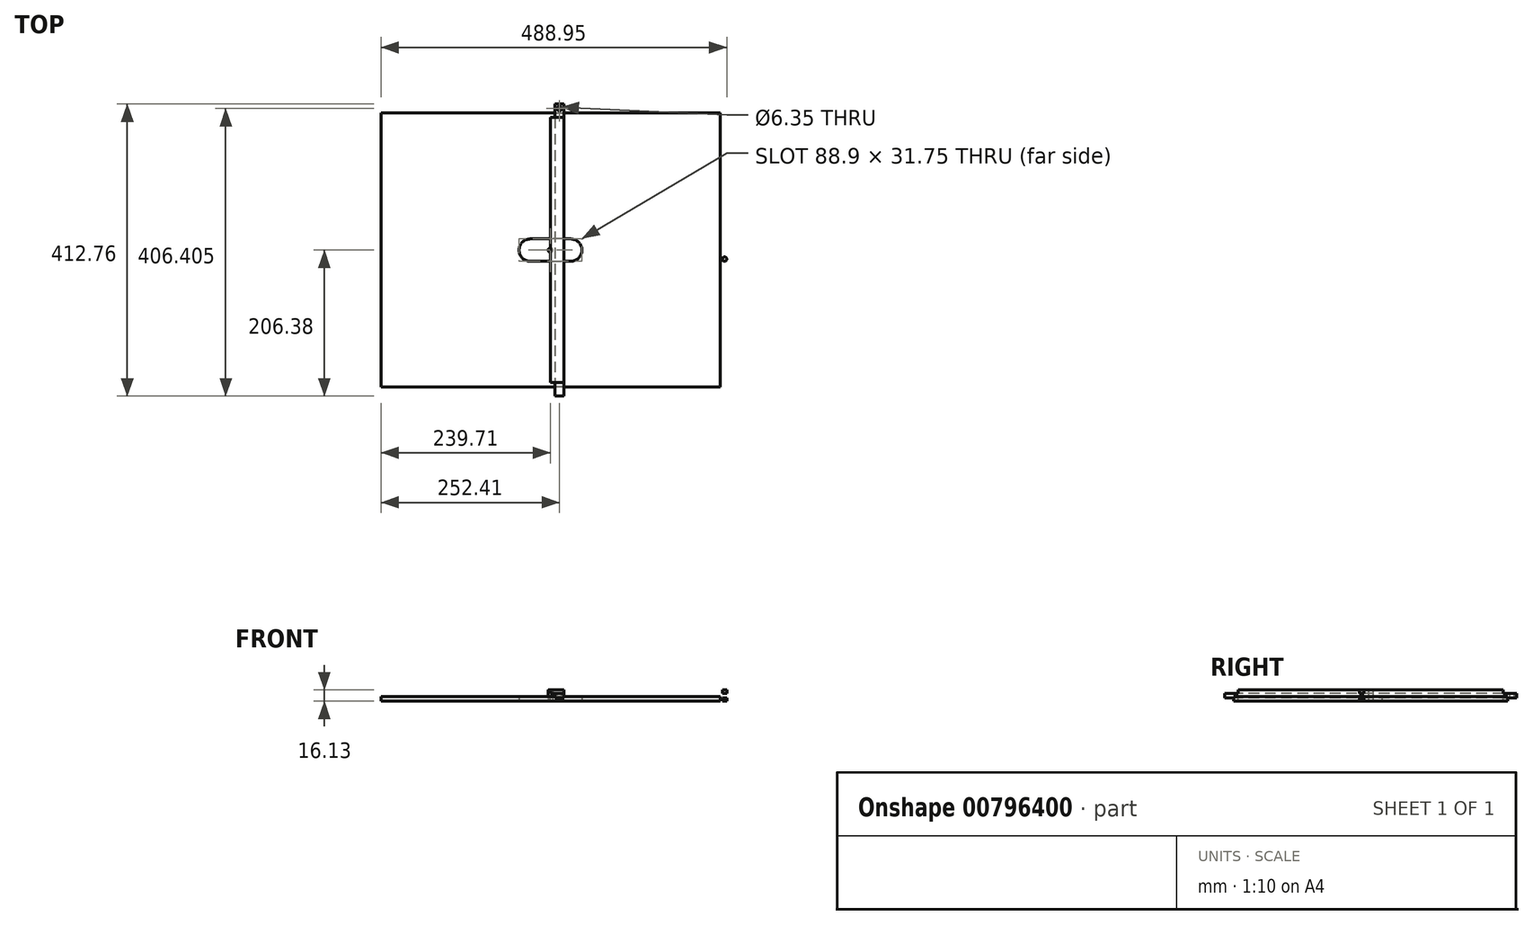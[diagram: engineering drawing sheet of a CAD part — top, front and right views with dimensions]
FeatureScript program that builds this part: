
annotation { "Feature Type Name" : "Feature", "Feature Type Description" : "" }
export const myFeature = defineFeature(function(context is Context, id is Id, definition is map)
    precondition{}
    {
        {
            var Q0;
            Q0=qCreatedBy(makeId("Front.planeOp"),FACE);
            var sketch = newSketch(context, id + "F0", { "sketchPlane" : qUnion([Q0])});
            skLineSegment(sketch, "E0", {"start": v(0, 0) * mm, "end": v(252.41, 0) * mm});
            skLineSegment(sketch, "E1", {"start": v(252.41, 0) * mm, "end": v(252.41, 4.76) * mm});
            skLineSegment(sketch, "E2", {"start": v(252.41, 4.76) * mm, "end": v(239.71, 4.76) * mm});
            skLineSegment(sketch, "E3", {"start": v(239.71, 4.76) * mm, "end": v(239.71, 11.11) * mm});
            skLineSegment(sketch, "E4", {"start": v(239.71, 11.11) * mm, "end": v(252.41, 11.11) * mm});
            skLineSegment(sketch, "E5", {"start": v(252.41, 11.11) * mm, "end": v(252.41, 15.87) * mm});
            skLineSegment(sketch, "E6", {"start": v(252.41, 15.87) * mm, "end": v(0, 15.87) * mm});
            skLineSegment(sketch, "E7.MirrorCS", {"start": v(-252.41, 15.87) * mm, "end": v(0, 15.87) * mm});
            skLineSegment(sketch, "E8.MirrorCS", {"start": v(-252.41, 11.11) * mm, "end": v(-252.41, 15.87) * mm});
            skLineSegment(sketch, "E9.MirrorCS", {"start": v(-239.71, 11.11) * mm, "end": v(-252.41, 11.11) * mm});
            skLineSegment(sketch, "E10.MirrorCS", {"start": v(-239.71, 4.76) * mm, "end": v(-239.71, 11.11) * mm});
            skLineSegment(sketch, "E11.MirrorCS", {"start": v(-252.41, 4.76) * mm, "end": v(-239.71, 4.76) * mm});
            skLineSegment(sketch, "E12.MirrorCS", {"start": v(-252.41, 0) * mm, "end": v(-252.41, 4.76) * mm});
            skLineSegment(sketch, "E13.MirrorCS", {"start": v(0, 0) * mm, "end": v(-252.41, 0) * mm});
            skSolve(sketch);
        }
        {
            var Q0;
            Q0=makeQuery(id+"F0.imprint","IMPRINT",FACE,{"disambiguationData":[TD([[makeQuery(id+"F0.imprint","IMPRINT",EDGE,{"derivedFrom":sQuery(id+"F0.wireOp",EDGE,"E0")}),1.0]])]});
            extrude(context, id + "F1", {"entities" : qUnion([Q0]), "depth" : 19.05 * mm, "offsetDistance" : 25.4 * mm});
        }
        {
            var Q0;
            Q0=makeQuery(id+"F1.opExtrude","SWEPT_FACE",FACE,{"disambiguationData":[OSD([sQuery(id+"F0.wireOp",EDGE,"E3")])]});
            var sketch = newSketch(context, id + "F2", { "sketchPlane" : qUnion([Q0])});
            skLineSegment(sketch, "E14", {"start": v(-6.35, 11.11) * mm, "end": v(-6.35, 4.76) * mm});
            skSolve(sketch);
        }
        {
            var Q0;
            {var subQ0=sQuery(id+"F2.wireOp",EDGE,"E14");Q0=makeQuery(id+"F2.imprint","IMPRINT",FACE,{"disambiguationData":[TD([[makeQuery(id+"F2.imprint","IMPRINT",EDGE,{"derivedFrom":subQ0}),1.0]])]});}
            extrude(context, id + "F3", {"entities" : qUnion([Q0]), "operationType" : NewBodyOperationType.REMOVE, "endBound" : BoundingType.THROUGH_ALL, "oppositeDirection" : true, "depth" : 25.4 * mm, "offsetDistance" : 25.4 * mm});
        }
        {
            var Q0;
            Q0=makeQuery(id+"F1.opExtrude","SWEPT_FACE",FACE,{"disambiguationData":[OSD([sQuery(id+"F0.wireOp",EDGE,"E6"),sQuery(id+"F0.wireOp",EDGE,"E7.MirrorCS")])]});
            var sketch = newSketch(context, id + "F4", { "sketchPlane" : qUnion([Q0])});
            skCircle(sketch, "E15", {"center": v(-246.06, -12.7) * mm, "radius": 3.18 * mm});
            skPoint(sketch, "E15.centerSnap0", {"position": v(-252.41, -12.7) * mm});
            skCircle(sketch, "E16.MirrorC", {"center": v(246.06, -12.7) * mm, "radius": 3.18 * mm});
            skSolve(sketch);
        }
        {
            var Q0;
            Q0=makeQuery(id+"F4.imprint","IMPRINT",FACE,{"disambiguationData":[TD([[makeQuery(id+"F4.imprint","IMPRINT",EDGE,{"derivedFrom":sQuery(id+"F4.wireOp",EDGE,"E15")}),1.0]])]});
            var Q1;
            Q1=makeQuery(id+"F4.imprint","IMPRINT",FACE,{"disambiguationData":[TD([[makeQuery(id+"F4.imprint","IMPRINT",EDGE,{"derivedFrom":sQuery(id+"F4.wireOp",EDGE,"E16.MirrorC")}),-1.0]])]});
            extrude(context, id + "F5", {"entities" : qUnion([Q0, Q1]), "operationType" : NewBodyOperationType.REMOVE, "endBound" : BoundingType.THROUGH_ALL, "oppositeDirection" : true, "depth" : 25.4 * mm, "offsetDistance" : 25.4 * mm});
        }
        {
            var Q0;
            Q0=qCreatedBy(makeId("Right.planeOp"),FACE);
            var sketch = newSketch(context, id + "F6", { "sketchPlane" : qUnion([Q0])});
            skLineSegment(sketch, "E17", {"start": v(0, 0) * mm, "end": v(187.32, 0) * mm});
            skLineSegment(sketch, "E18", {"start": v(187.33, 0) * mm, "end": v(187.33, 4.76) * mm});
            skLineSegment(sketch, "E19", {"start": v(187.33, 4.76) * mm, "end": v(206.38, 4.76) * mm});
            skLineSegment(sketch, "E20", {"start": v(206.38, 4.76) * mm, "end": v(206.38, 11.11) * mm});
            skLineSegment(sketch, "E21", {"start": v(206.38, 11.11) * mm, "end": v(187.33, 11.11) * mm});
            skLineSegment(sketch, "E22", {"start": v(187.33, 11.11) * mm, "end": v(187.33, 16.13) * mm});
            skLineSegment(sketch, "E23", {"start": v(187.32, 16.13) * mm, "end": v(0, 16.13) * mm});
            skLineSegment(sketch, "E24.MirrorCS", {"start": v(-187.33, 16.13) * mm, "end": v(0, 16.13) * mm});
            skLineSegment(sketch, "E25.MirrorCS", {"start": v(0, 0) * mm, "end": v(-187.33, 0) * mm});
            skLineSegment(sketch, "E26.MirrorCS", {"start": v(-187.33, 0) * mm, "end": v(-187.33, 4.76) * mm});
            skLineSegment(sketch, "E27.MirrorCS", {"start": v(-187.33, 11.11) * mm, "end": v(-187.33, 16.13) * mm});
            skLineSegment(sketch, "E28.MirrorCS", {"start": v(-206.38, 11.11) * mm, "end": v(-187.33, 11.11) * mm});
            skLineSegment(sketch, "E29.MirrorCS", {"start": v(-187.33, 4.76) * mm, "end": v(-206.38, 4.76) * mm});
            skLineSegment(sketch, "E30.MirrorCS", {"start": v(-206.38, 4.76) * mm, "end": v(-206.38, 11.11) * mm});
            skSolve(sketch);
        }
        {
            var Q0;
            Q0=makeQuery(id+"F6.imprint","IMPRINT",FACE,{"disambiguationData":[TD([[makeQuery(id+"F6.imprint","IMPRINT",EDGE,{"derivedFrom":sQuery(id+"F6.wireOp",EDGE,"E17")}),1.0]])]});
            extrude(context, id + "F7", {"entities" : qUnion([Q0]), "depth" : 19.05 * mm, "offsetDistance" : 25.4 * mm});
        }
        {
            var Q0;
            Q0=makeQuery(id+"F7.opExtrude","SWEPT_FACE",FACE,{"disambiguationData":[OSD([sQuery(id+"F6.wireOp",EDGE,"E21")])]});
            var sketch = newSketch(context, id + "F8", { "sketchPlane" : qUnion([Q0])});
            skCircle(sketch, "E31", {"center": v(12.7, 200.03) * mm, "radius": 3.18 * mm});
            skPoint(sketch, "E31.centerSnap0", {"position": v(3.17, 200.03) * mm});
            skPoint(sketch, "E31.centerSnap1", {"position": v(12.7, 209.55) * mm});
            skCircle(sketch, "E32.MirrorC", {"center": v(12.7, -200.03) * mm, "radius": 3.18 * mm});
            skSolve(sketch);
        }
        {
            var Q0;
            Q0=makeQuery(id+"F8.imprint","IMPRINT",FACE,{"disambiguationData":[TD([[makeQuery(id+"F8.imprint","IMPRINT",EDGE,{"derivedFrom":sQuery(id+"F8.wireOp",EDGE,"E31")}),1.0]])]});
            var Q1;
            Q1=makeQuery(id+"F8.imprint","IMPRINT",FACE,{"disambiguationData":[TD([[makeQuery(id+"F8.imprint","IMPRINT",EDGE,{"derivedFrom":sQuery(id+"F8.wireOp",EDGE,"E32.MirrorC")}),-1.0]])]});
            extrude(context, id + "F9", {"entities" : qUnion([Q0, Q1]), "operationType" : NewBodyOperationType.REMOVE, "endBound" : BoundingType.THROUGH_ALL, "oppositeDirection" : true, "depth" : 25.4 * mm, "offsetDistance" : 25.4 * mm});
        }
        {
            var Q0;
            Q0=makeQuery(id+"F7.opExtrude","SWEPT_FACE",FACE,{"disambiguationData":[OSD([sQuery(id+"F6.wireOp",EDGE,"E30.MirrorCS")])]});
            var sketch = newSketch(context, id + "F10", { "sketchPlane" : qUnion([Q0])});
            skLineSegment(sketch, "E33", {"start": v(6.35, 11.11) * mm, "end": v(6.35, 4.76) * mm});
            skSolve(sketch);
        }
        {
            var Q0;
            {var subQ0=sQuery(id+"F10.wireOp",EDGE,"E33");Q0=makeQuery(id+"F10.imprint","IMPRINT",FACE,{"disambiguationData":[TD([[makeQuery(id+"F10.imprint","IMPRINT",EDGE,{"derivedFrom":subQ0}),-1.0]])]});}
            extrude(context, id + "F11", {"entities" : qUnion([Q0]), "operationType" : NewBodyOperationType.REMOVE, "endBound" : BoundingType.THROUGH_ALL, "oppositeDirection" : true, "depth" : 25.4 * mm, "offsetDistance" : 25.4 * mm});
        }
        {
            var Q0;
            Q0=qCreatedBy(makeId("Top.planeOp"),FACE);
            var sketch = newSketch(context, id + "F12", { "sketchPlane" : qUnion([Q0])});
            skLineSegment(sketch, "E34", {"start": v(0, 193.68) * mm, "end": v(239.71, 193.68) * mm});
            skLineSegment(sketch, "E35", {"start": v(239.71, 193.68) * mm, "end": v(239.71, 0) * mm});
            skLineSegment(sketch, "E36.MirrorCS", {"start": v(0, -193.68) * mm, "end": v(239.71, -193.68) * mm});
            skLineSegment(sketch, "E37.MirrorCS", {"start": v(239.71, -193.68) * mm, "end": v(239.71, 0) * mm});
            skLineSegment(sketch, "E38.MirrorCS", {"start": v(0, 193.68) * mm, "end": v(-239.71, 193.68) * mm});
            skLineSegment(sketch, "E39.MirrorCS", {"start": v(-239.71, 193.68) * mm, "end": v(-239.71, 0) * mm});
            skLineSegment(sketch, "E40.MirrorCS", {"start": v(-239.71, -193.68) * mm, "end": v(-239.71, 0) * mm});
            skLineSegment(sketch, "E41.MirrorCS", {"start": v(0, -193.68) * mm, "end": v(-239.71, -193.68) * mm});
            skLineSegment(sketch, "E42", {"start": v(0, 15.88) * mm, "end": v(28.57, 15.88) * mm});
            skLineSegment(sketch, "E43", {"start": v(44.45, 0) * mm, "end": v(44.45, 0) * mm});
            skLineSegment(sketch, "E44.MirrorCS", {"start": v(0, -15.88) * mm, "end": v(28.58, -15.88) * mm});
            skLineSegment(sketch, "E45.MirrorCS", {"start": v(0, 15.88) * mm, "end": v(-28.58, 15.88) * mm});
            skLineSegment(sketch, "E46.MirrorCS", {"start": v(-44.45, 0) * mm, "end": v(-44.45, 0) * mm});
            skLineSegment(sketch, "E47.MirrorCS", {"start": v(0, -15.87) * mm, "end": v(-28.58, -15.88) * mm});
            skPoint(sketch, "E48.visualSharp", {"position": v(-44.45, 15.88) * mm});
            skArc(sketch, "E48.filletArc", {"start": v(-28.58, 15.88) * mm, "mid": v(-39.8, 11.23) * mm, "end": v(-44.45, 0) * mm});
            skPoint(sketch, "E49.visualSharp", {"position": v(-44.45, -15.88) * mm});
            skArc(sketch, "E49.filletArc", {"start": v(-44.45, 0) * mm, "mid": v(-39.8, -11.23) * mm, "end": v(-28.58, -15.88) * mm});
            skPoint(sketch, "E50.visualSharp", {"position": v(44.45, -15.88) * mm});
            skArc(sketch, "E50.filletArc", {"start": v(28.58, -15.88) * mm, "mid": v(39.8, -11.23) * mm, "end": v(44.45, 0) * mm});
            skPoint(sketch, "E51.visualSharp", {"position": v(44.45, 15.88) * mm});
            skArc(sketch, "E51.filletArc", {"start": v(44.45, 0) * mm, "mid": v(39.8, 11.23) * mm, "end": v(28.57, 15.88) * mm});
            skSolve(sketch);
        }
        {
            var Q0;
            Q0=makeQuery(id+"F12.imprint","IMPRINT",FACE,{"disambiguationData":[TD([[makeQuery(id+"F12.imprint","IMPRINT",EDGE,{"derivedFrom":sQuery(id+"F12.wireOp",EDGE,"E34")}),-1.0]])]});
            extrude(context, id + "F13", {"entities" : qUnion([Q0]), "depth" : 6.35 * mm, "offsetDistance" : 25.4 * mm});
        }
        {
            var Q0;
            Q0=qCreatedBy(makeId("Top.planeOp"),FACE);
            var sketch = newSketch(context, id + "F14", { "sketchPlane" : qUnion([Q0])});
            skCircle(sketch, "E52", {"center": v(0, 0) * mm, "radius": 3.18 * mm});
            skSolve(sketch);
        }
        {
            var Q0;
            Q0=makeQuery(id+"F14.imprint","IMPRINT",FACE,{"disambiguationData":[TD([[makeQuery(id+"F14.imprint","IMPRINT",EDGE,{"derivedFrom":sQuery(id+"F14.wireOp",EDGE,"E52")}),1.0]])]});
            extrude(context, id + "F15", {"entities" : qUnion([Q0]), "depth" : 15.88 * mm, "offsetDistance" : 25.4 * mm});
        }
    });
